# Revit family: 203_GBL-_
name_source: partatom
category: Duct Accessories
units: mm (PartAtom-declared; Revit-internal decimal feet)

## family parameters
Always vertical = Yes
Cut with Voids When Loaded = No
Part Type = Damper
Round Connector Dimension = Use Diameter
Shared = No
Work Plane-Based = No

## types (12) — shared parameters
CAT0 = Yes
Description = REGULATING AND MEASURING LENS DAMPER
Manufacturer = Alnor
QmdConnectorList = 201;D;202;D
URL = http://www.ventilation-alnor.co.uk
magiPartTypeId = 203
magiProductFamilyId = GBL-*

## per-type parameters (varying)
| type | BD | D | H2D | L1 | L2 | L2D | LL | R | W2D |
| GBL-80 | 125 mm  [stored 0.410105 ft] | 80 mm | 80 mm  [stored 0.262467 ft] | 28 mm | 41 mm | 110 mm | 55 mm  [stored 0.180446 ft] | 40 mm  [stored 0.131234 ft] | 80 mm  [stored 0.262467 ft] |
| GBL-800 | 1015 mm | 800 mm | 800 mm | 68 mm | 101 mm | 270 mm | 135 mm | 400 mm | 800 mm |
| GBL-630 | 815 mm | 630 mm | 630 mm | 43 mm | 64 mm | 170 mm | 85 mm | 315 mm | 630 mm |
| GBL-500 | 655 mm | 500 mm | 500 mm | 43 mm | 64 mm | 170 mm | 85 mm | 250 mm | 500 mm |
| GBL-400 | 525 mm | 400 mm | 400 mm | 48 mm | 71 mm | 190 mm | 95 mm | 200 mm | 400 mm |
| GBL-315 | 410 mm | 315 mm | 315 mm | 34 mm | 51 mm | 135 mm | 68 mm | 158 mm | 315 mm |
| GBL-250 | 335 mm | 250 mm | 250 mm | 34 mm | 51 mm | 135 mm | 68 mm | 125 mm  [stored 0.410105 ft] | 250 mm |
| GBL-200 | 285 mm | 200 mm | 200 mm | 28 mm | 41 mm | 110 mm | 55 mm  [stored 0.180446 ft] | 100 mm  [stored 0.328084 ft] | 200 mm |
| GBL-160 | 230 mm | 160 mm | 160 mm | 28 mm | 41 mm | 110 mm | 55 mm  [stored 0.180446 ft] | 80 mm  [stored 0.262467 ft] | 160 mm |
| GBL-150 | 230 mm | 150 mm | 150 mm | 53 mm | 79 mm | 210 mm | 105 mm | 75 mm | 150 mm |
| GBL-125 | 188 mm | 125 mm | 125 mm  [stored 0.410105 ft] | 28 mm | 41 mm | 110 mm | 55 mm  [stored 0.180446 ft] | 63 mm | 125 mm  [stored 0.410105 ft] |
| GBL-100 | 165 mm | 100 mm | 100 mm  [stored 0.328084 ft] | 28 mm | 41 mm | 110 mm | 55 mm  [stored 0.180446 ft] | 50 mm | 100 mm  [stored 0.328084 ft] |

note: column(s) folded — value = type name in every type: MC Product Code, magiProductId

note: [stored X ft] marks values corroborated as IEEE doubles in the binary element streams (Revit-internal decimal feet)

## geometry (parser evidence)
native form markers: Blend x4, Sweep x2
no freeform markers — native parametric forms only
